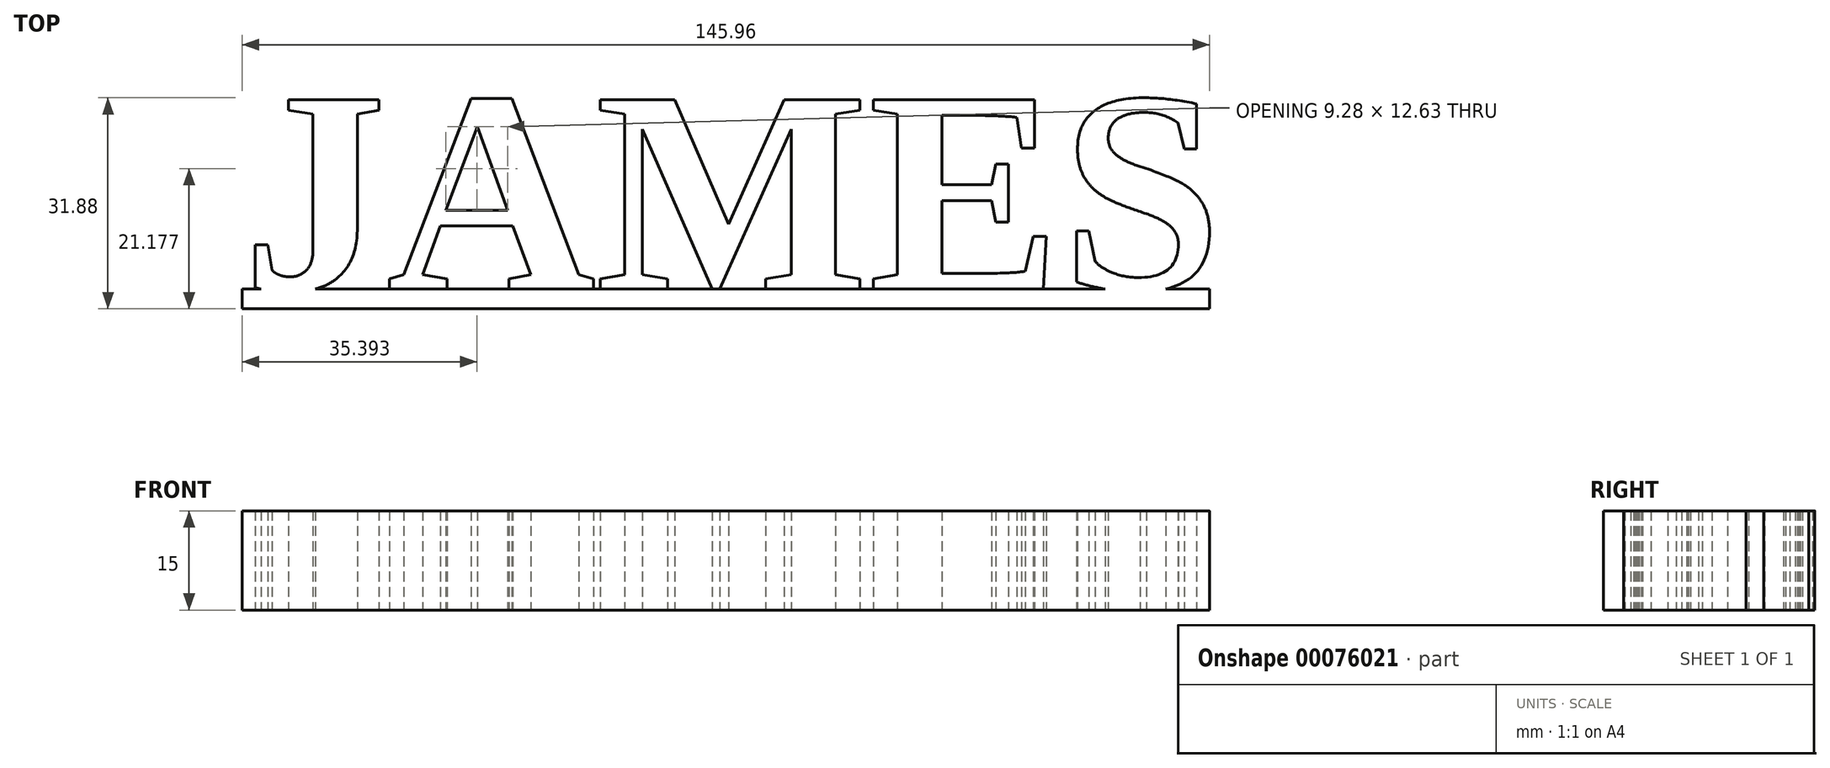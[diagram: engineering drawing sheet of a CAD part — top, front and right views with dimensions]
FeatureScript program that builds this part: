
annotation { "Feature Type Name" : "Feature", "Feature Type Description" : "" }
export const myFeature = defineFeature(function(context is Context, id is Id, definition is map)
    precondition{}
    {
        {
            var Q0;
            Q0=qCreatedBy(makeId("Top.planeOp"),FACE);
            var sketch = newSketch(context, id + "F0", { "sketchPlane" : qUnion([Q0])});
            skText(sketch, "E0", { "text": "JAMES", "fontName": "Tinos-Bold.ttf"});
            skLineSegment(sketch, "E1.bottom", {"start": v(-77.7, -14.92) * mm, "end": v(68.26, -14.92) * mm});
            skLineSegment(sketch, "E1.top", {"start": v(-77.7, -17.92) * mm, "end": v(68.26, -17.92) * mm});
            skLineSegment(sketch, "E1.left", {"start": v(-77.7, -14.92) * mm, "end": v(-77.7, -17.92) * mm});
            skLineSegment(sketch, "E1.right", {"start": v(68.26, -14.92) * mm, "end": v(68.26, -17.92) * mm});
            const initialGuessF0  = {"E0": [-0.0777, -0.01492, 1, 0, 0.0314]};
            skSetInitialGuess(sketch, initialGuessF0);
            skSolve(sketch);
        }
        {
            var Q0;
            Q0 = qSketchRegion(id + "F0", true);
            extrude(context, id + "F1", {"entities" : qUnion([Q0]), "depth" : 15 * mm});
        }
    });
